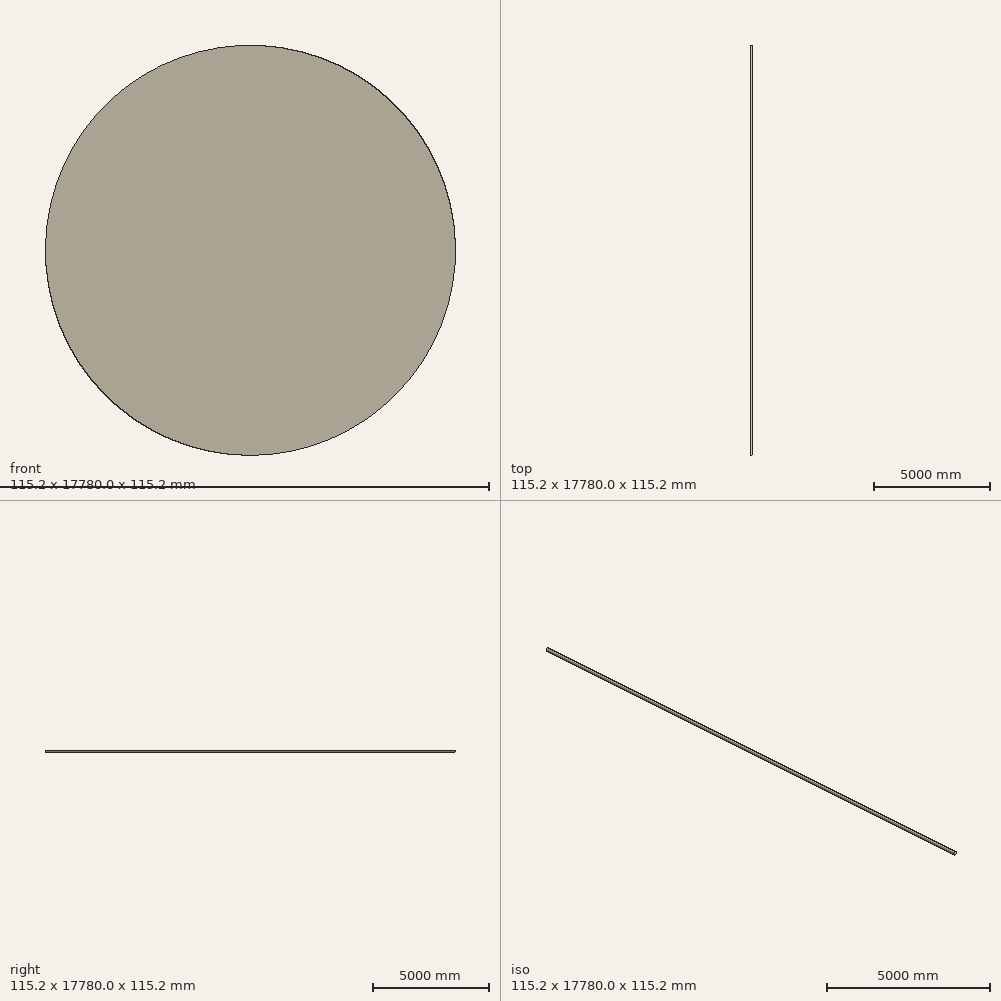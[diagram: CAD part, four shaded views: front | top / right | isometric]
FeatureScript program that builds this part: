
annotation { "Feature Type Name" : "Feature", "Feature Type Description" : "" }
export const myFeature = defineFeature(function(context is Context, id is Id, definition is map)
    precondition{}
    {
        {
            var Q0;
            Q0=qCreatedBy(makeId("Front.planeOp"),FACE);
            var sketch = newSketch(context, id + "F0", { "sketchPlane" : qUnion([Q0])});
            skCircle(sketch, "E0", {"center": v(0, 0) * mm, "radius": 34.9 * mm});
            skSolve(sketch);
        }
        {
            var Q0;
            Q0=makeQuery(id+"F0.imprint","IMPRINT",FACE,{"disambiguationData":[TD([[makeQuery(id+"F0.imprint","IMPRINT",EDGE,{"derivedFrom":sQuery(id+"F0.wireOp",EDGE,"E0")}),1.0]])]});
            extrude(context, id + "F1", {"entities" : qUnion([Q0]), "depth" : 76.2 * mm});
        }
        {
            var Q0;
            Q0=qCreatedBy(makeId("Front.planeOp"),FACE);
            var sketch = newSketch(context, id + "F2", { "sketchPlane" : qUnion([Q0])});
            skCircle(sketch, "E1", {"center": v(0, 0) * mm, "radius": 57.6 * mm});
            skSolve(sketch);
        }
        {
            var Q0;
            Q0=makeQuery(id+"F2.imprint","IMPRINT",FACE,{"disambiguationData":[TD([[makeQuery(id+"F2.imprint","IMPRINT",EDGE,{"derivedFrom":sQuery(id+"F2.wireOp",EDGE,"E1")}),1.0]])]});
            extrude(context, id + "F3", {"entities" : qUnion([Q0]), "operationType" : NewBodyOperationType.ADD, "depth" : 17780 * mm});
        }
    });
